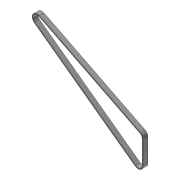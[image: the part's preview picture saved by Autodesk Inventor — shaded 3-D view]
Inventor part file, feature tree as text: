
AUTODESK INVENTOR PART (.ipt)
format: ipt  version: 2012 (Build 160160000, 160)  size: 84,992 bytes
history: native  units: in
note: dims shown in document units (in); Inventor stores cm internally (conversion verified against a paired STEP export)
features: extrude x1, sketch x1
ambient origin geometry x8: Origin, YZ Plane, XZ Plane, XY Plane, X Axis, Y Axis, Z Axis, Center Point
bodies: Solid1 (feature_tree)
feature tree (2):
  extrude  "Extrusion1"  Depth=0.125in
  sketch  "Sketch1"  dims[d0=0.4375in d1=0.125in d2=0.4in d3=0.0in]
